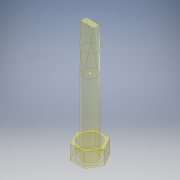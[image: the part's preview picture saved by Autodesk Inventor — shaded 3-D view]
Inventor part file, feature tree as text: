
AUTODESK INVENTOR PART (.ipt)
format: ipt  version: 2017 (Build 210142000, 142)  size: 179,200 bytes
history: native  units: mm
features: sketch x9, extrude x2, plane x2, loft x2, other x2
ambient origin geometry x8: Origin, YZ Plane, XZ Plane, XY Plane, X Axis, Y Axis, Z Axis, Center Point
bodies: Solid1 (feature_tree)
feature tree (17):
  extrude  "Extrusion1"  Depth=5.0mm TaperAngle=0.0deg
  extrude  "Extrusion2"  Depth=5.0mm TaperAngle=0.0deg
  plane  "Work Plane1"
  sketch  "Sketch5"  dims[d8=7.5mm d30=0.0mm d31=90.0deg]
  sketch  "Sketch6"  dims[d32=0.0mm d33=90.0deg d34=0.0mm d35=90.0deg]
  loft  "Loft3"
  plane  "Work Plane3"
  loft  "Loft4"
  sketch  "Sketch1"  dims[d2=7.0mm d3=5.0mm d4=0.0mm]
  sketch  "Sketch4"  dims[d5=5.0mm d6=25.0mm d7=0.0mm]
  sketch  "3D Sketch12"
  sketch  "3D Sketch13"
  sketch  "3D Sketch14"
  sketch  "3D Sketch15"
  other  "Edges3"
  sketch  "Sketch8"  dims[d36=0.0mm d37=90.0deg d38=0.0mm d39=90.0deg d40=0.0mm d41=90.0deg d42=7.5mm d44=0.0mm d45=90.0deg d46=0.0mm d47=90.0deg]
  other  "Edges4"
